# Revit family: Normann_ENTRY_ETR10A-R290
name_source: partatom
category: Attrezzature speciali
units: mm (PartAtom-declared; Revit-internal decimal feet)

## family parameters
Basato su piano di lavoro = No
Condiviso = No
Punto di calcolo locali = No
Quota connettore circolare = Usa diametro
Sempre verticale = Sì
Taglio con vuoti quando caricato = No
Tipo di parte = Normale

## types (4) — shared parameters
Asset Identifier = ETR10A-R290
Capacity internal - L = 199
Condensation = AIR
Controller = EVJ805
Depth Actual = 695 mm  [stored 2.28018 ft]
Depth Body = 695 mm  [stored 2.28018 ft]
Door Side R_L = No
Door_DX = No
Door_SX = Sì
GWP = 3
Gross Weight kg = 139
H_Feet_Limits = 125 mm  [stored 0.410105 ft]
Height_Door = 710 mm  [stored 2.3294 ft]
Height_Feet_100to160 = 125 mm  [stored 0.410105 ft]
Ice cream pan 5l quantity (360x165x120mm) = 15
Internal depth actual - mm = 417 mm  [stored 1.36811 ft]
Internal height actual - mm = 775 mm  [stored 2.54265 ft]
Internal length actual - mm = 615 mm  [stored 2.01772 ft]
Length Actual = 715 mm  [stored 2.3458 ft]
Manufacturer = Normann
Mat_Frame = Acciaio inox, spazzolato
Mat_Grid = Acciaio inox, spazzolato
Max current cold cycle - A = 6.13
Max power cold cycle - W = 1531
Model Category = Blast chiller reach-in
Model Series = Entry
Net Weight kg = 124
OffSet_Display = 68 mm
Optional = CORE PROBE
Packaging depth actual - mm = 755 mm  [stored 2.47703 ft]
Packaging height actual - mm = 1555 mm  [stored 5.10171 ft]
Packaging length actual - mm = 730 mm  [stored 2.39501 ft]
Packing volume - m3 = 0.9
Power Supply (Volts/Ph/Hz) = 220-240/1N/50
Refrigerant gas = R290
Refrigeration Climate Class = 4
Temperature range - °C = -40/+3
Tray Type = GN1/1 e EN1
Tray number = 10
URL Manufacturer = https://www.normann.it
Yield per blast chiling cycle (+90°C/+3°C) - kg = 32
Yield per blast chiling cycle +65/+10°C (EN22042) - kg = 27
Yield per blast chiling cycle consumption (EN22042) - kWh = 2
Yield per blast chiling cycle energy consumed (EN22042) - kWh/kg = 0.099
Yield per blast chiling cycle test time (EN22042) - min = 96
Yield per shock freezing cycle (+90/-18°C) - kg = 22
Yield per shock freezing cycle +65/-18°C (EN22042) - kg = 17
Yield per shock freezing cycle consuption (EN22042) - kWh = 4
Yield per shock freezing cycle energy consumed (EN22042) - kWh/kg = 0.286
Yield per shock freezing cycle test time (EN22042) - min = 264
zero-valued in all types: Liquid line diameter - mm, Max current warm cycle - A, Max power warm cycle - W, Prospetto di default, Suction line diameter - mm, Tray quantity EN1-GN1/1 h20mm, Tray quantity EN1-GN1/1 h40mm, Tray quantity EN1-GN1/1 h65mm, Tray quantity GN2/3 h65mm

## per-type parameters (varying)
| type | Feet | Height Actual | Height_Feet_Actual | ID | Wheel | Wheel_Feet |
| ENTRY10 AIR, R290, 220-240/1N/50, EVJ805, LHH, FEET | Sì | 1412 mm  [stored 4.63255 ft] | 125 mm  [stored 0.410105 ft] | 5A1D1D3B1-10A1B | No | No |
| ENTRY10 AIR, R290, 220-240/1N/50, EVJ805, LHH, WHEELS | No | 1396 mm  [stored 4.58005 ft] | 100 mm  [stored 0.328084 ft] | 5A1D1D3B1-10A1D | Sì | Sì |
| ENTRY10 AIR, R290, 220-240/1N/50, EVJ805, RHH, FEET | Sì | 1412 mm  [stored 4.63255 ft] | 125 mm  [stored 0.410105 ft] | 5A1D1D3B1-10A2B | No | No |
| ENTRY10 AIR, R290, 220-240/1N/50, EVJ805, RHH, WHEELS | No | 1396 mm  [stored 4.58005 ft] | 100 mm  [stored 0.328084 ft] | 5A1D1D3B1-10A2D | Sì | Sì |

note: [stored X ft] marks values corroborated as IEEE doubles in the binary element streams (Revit-internal decimal feet)
